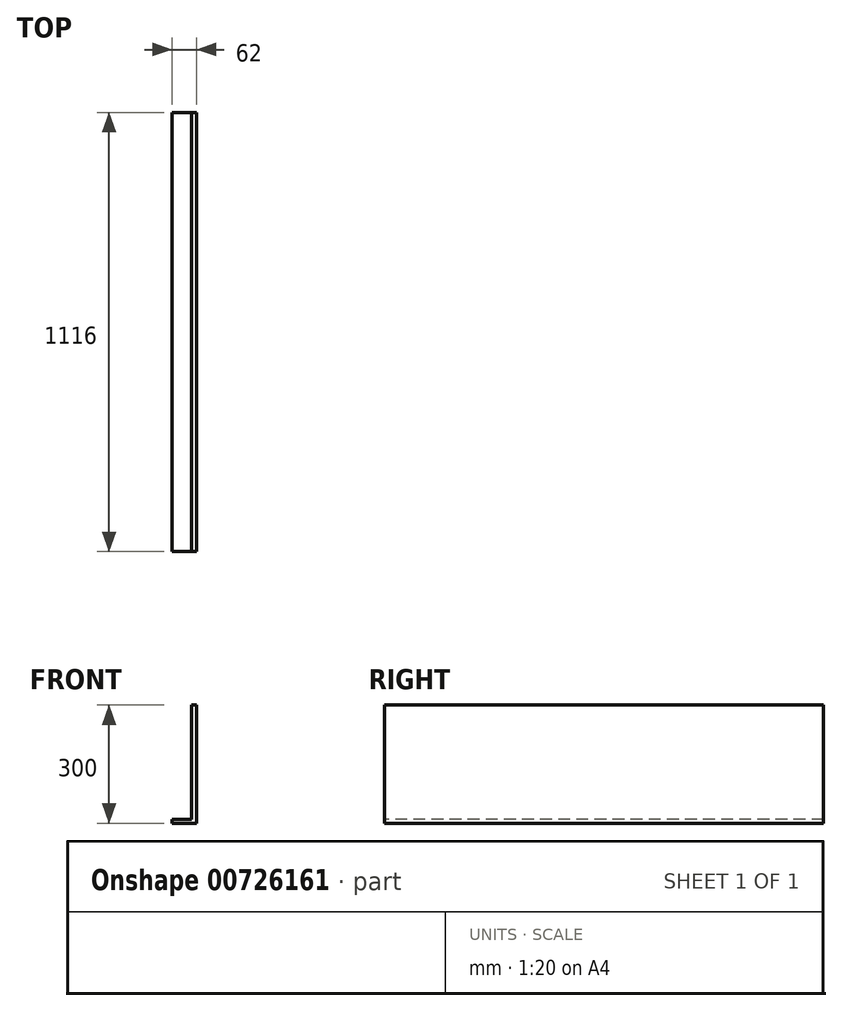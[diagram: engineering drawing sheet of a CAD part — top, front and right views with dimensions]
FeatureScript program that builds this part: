
annotation { "Feature Type Name" : "Feature", "Feature Type Description" : "" }
export const myFeature = defineFeature(function(context is Context, id is Id, definition is map)
    precondition{}
    {
        {
            var Q0;
            Q0=qCreatedBy(makeId("Right.planeOp"),FACE);
            var sketch = newSketch(context, id + "F0", { "sketchPlane" : qUnion([Q0])});
            skLineSegment(sketch, "E0.bottom", {"start": v(-558, 150) * mm, "end": v(558, 150) * mm});
            skLineSegment(sketch, "E0.top", {"start": v(-558, -150) * mm, "end": v(558, -150) * mm});
            skLineSegment(sketch, "E0.left", {"start": v(-558, 150) * mm, "end": v(-558, -150) * mm});
            skLineSegment(sketch, "E0.right", {"start": v(558, 150) * mm, "end": v(558, -150) * mm});
            skLineSegment(sketch, "E1", {"start": v(-558, 0) * mm, "end": v(558, 0) * mm, "construction": true});
            skSolve(sketch);
        }
        {
            var Q0;
            Q0 = qSketchRegion(id + "F0", true);
            extrude(context, id + "F1", {"entities" : qUnion([Q0]), "depth" : 12 * mm, "offsetDistance" : 25 * mm});
        }
        {
            var Q0;
            Q0=makeQuery(id+"F1.opExtrude","CAP_FACE",FACE,{"disambiguationData":[OSD([sQuery(id+"F0.wireOp",EDGE,"E0.bottom"),sQuery(id+"F0.wireOp",EDGE,"E0.top"),sQuery(id+"F0.wireOp",EDGE,"E0.left"),sQuery(id+"F0.wireOp",EDGE,"E0.right")])],"isStart":true});
            var sketch = newSketch(context, id + "F2", { "sketchPlane" : qUnion([Q0])});
            skLineSegment(sketch, "E2.bottom", {"start": v(-558, -150) * mm, "end": v(558, -150) * mm});
            skLineSegment(sketch, "E2.top", {"start": v(-558, -140) * mm, "end": v(558, -140) * mm});
            skLineSegment(sketch, "E2.left", {"start": v(-558, -150) * mm, "end": v(-558, -140) * mm});
            skLineSegment(sketch, "E2.right", {"start": v(558, -150) * mm, "end": v(558, -140) * mm});
            skSolve(sketch);
        }
        {
            var Q0;
            Q0 = qSketchRegion(id + "F2", true);
            extrude(context, id + "F3", {"entities" : qUnion([Q0]), "operationType" : NewBodyOperationType.ADD, "depth" : 50 * mm, "offsetDistance" : 25 * mm});
        }
    });
